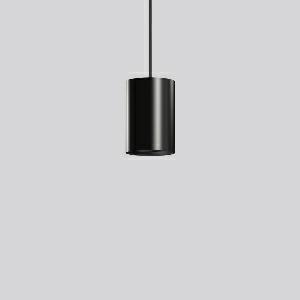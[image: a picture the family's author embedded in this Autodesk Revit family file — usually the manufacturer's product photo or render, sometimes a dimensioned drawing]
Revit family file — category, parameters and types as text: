
# Revit family: deecos_p_maxi_911542_003_2_626c
name_source: partatom
category: Lighting Fixtures
units: mm (PartAtom-declared; Revit-internal decimal feet)

## family parameters
Cut with Voids When Loaded = No
Host = Face
Light Source = No
Part Type = Normal
Room Calculation Point = No
Round Connector Dimension = Use Diameter
Shared = No

## types (1)
- DEECOS P maxi (1 x LED Modul 927, 3450 lm, 2700)
    Apparent Load = 35 VA
    Approval mark = CE
    CIE Flux Codes = 96 100 100 100 100
    Color Rendering = 92
    Color Temperature = 2700
    Default Elevation = 1800 mm
    Description = Series: DEECOS P maxi
Cylindrical pendant luminaire. Housing: die-cast aluminium, powder-coated. Canopy made of powder-coated sheet steel with magnetic attachment. Optical assembly with lens made of plastic (polycarbonate) for the best homogeneous light distribution - can be changed without tools. Best colour rendering index Ra>90. Transparent suspension cable 2 m, can be shortened. High quality converter without flickering and stroboscopic effect. The following accessories can be mounted without use of tools: interchangeable lenses, honeycomb louvre, clear and frosted diffusers, white interchangeable plastic ring. Decorative recessed suspension set available as accessory. 
Colour: deep black, matt (RAL 9005)
Diameter: 123 mm
Height: 181 mm
Suspension length: 2000 mm
Lamp: LED
Socket: without socket
Colour temperature: 2700K
Colour rendering index (CRI): 92
System power: 35 W
Rated luminous flux: 3450 lm
Luminous efficiency: 99 lm/W
Control gear: Regulated power supply
Protection class: I
Type of protection: IP 20
    Height = 181 mm
    Lamp = 1 x LED Modul 927
    Lamp Light Flux = 3450 lm
    Lamp count = 1
    Length = 123 mm
    Lifetime = 50000 h
    Luminous efficacy = 99 lm/W
    Manufacturer = RZB
    ModVariant = No
    Model = 911542.003.2
    Mounting Place = Ceiling
    Mounting Type = Pendant
    Number of Poles = 1
    OnlyDefault = Yes
    Power Factor = 1
    Product Name = DEECOS P maxi
    Product group = Pendant luminaires
    ProductGroupID = 902
    Protection Class = Protection class I
    Protection Degree = IP 20
    RLX_Detail_Level = 1
    RLX_Emergency_Light_Flux = 0 lm
    RLX_Emergency_Type = 0
    RLX_Emergency_Type_DB = No
    RlxData = <blob elided: 36425 chars, md5=ea14ce5c>
    Socket = socket
    Standby Power = 0 W
    System Light Flux = 3450 lm
    System Power = 35 W
    Type Comments = Product without accessories
    Type Image = 911480.003.jpg
    URL = http://relux.com
    VarID = ---
    Voltage = 230 V
    Voltage Range = 220-240 V
    Weight = 0.00 kg
    Width = 0 mm  [stored 0 ft]

note: [stored X ft] marks values corroborated as IEEE doubles in the binary element streams (Revit-internal decimal feet)

## geometry (parser evidence)
native form markers: Blend x4, Sweep x10
no freeform markers — native parametric forms only
